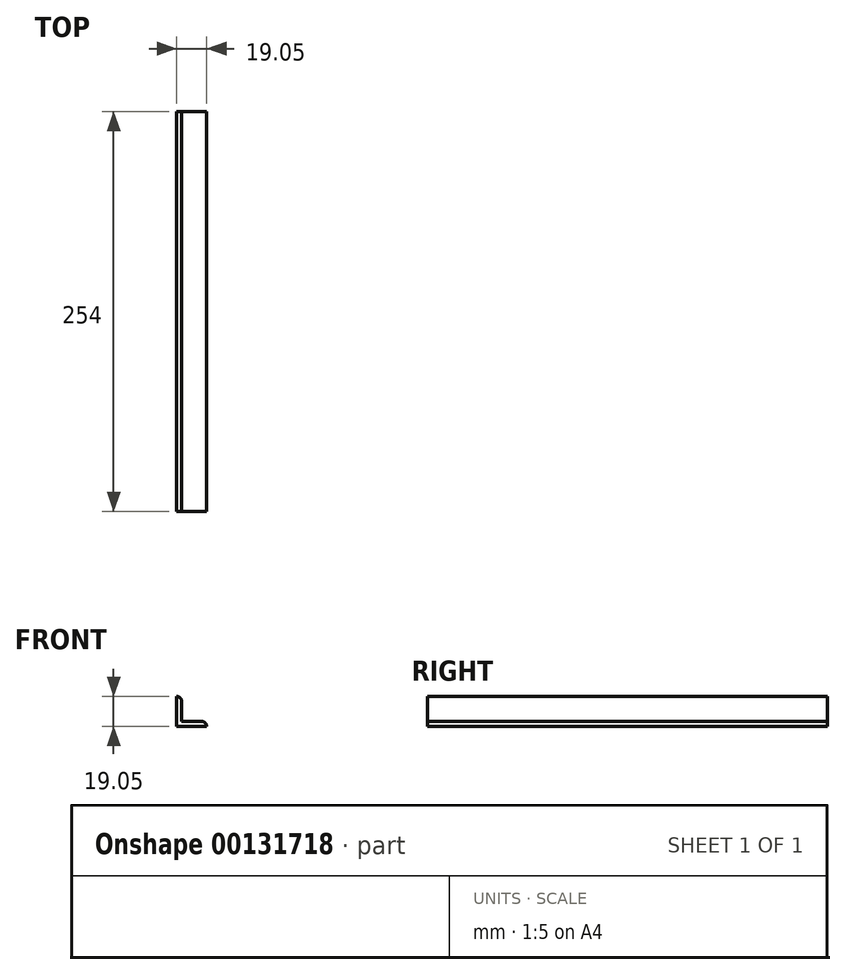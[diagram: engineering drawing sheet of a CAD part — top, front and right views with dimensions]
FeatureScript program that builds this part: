
annotation { "Feature Type Name" : "Feature", "Feature Type Description" : "" }
export const myFeature = defineFeature(function(context is Context, id is Id, definition is map)
    precondition{}
    {
        {
            var Q0;
            Q0=qCreatedBy(makeId("Front.planeOp"),FACE);
            var sketch = newSketch(context, id + "F0", { "sketchPlane" : qUnion([Q0])});
            skLineSegment(sketch, "E0", {"start": v(0, 19.05) * mm, "end": v(0, 0) * mm});
            skLineSegment(sketch, "E1", {"start": v(0, 0) * mm, "end": v(19.05, 0) * mm});
            skLineSegment(sketch, "E2", {"start": v(15.88, 3.17) * mm, "end": v(3.18, 3.17) * mm});
            skLineSegment(sketch, "E3", {"start": v(3.17, 3.17) * mm, "end": v(3.17, 15.88) * mm});
            skLineSegment(sketch, "E4", {"start": v(0, 19.05) * mm, "end": v(0, 19.05) * mm});
            skArc(sketch, "E5.filletArc", {"start": v(3.17, 15.88) * mm, "mid": v(2.25, 18.12) * mm, "end": v(0, 19.05) * mm});
            skArc(sketch, "E6.filletArc", {"start": v(19.05, 0) * mm, "mid": v(18.12, 2.25) * mm, "end": v(15.88, 3.18) * mm});
            skSolve(sketch);
        }
        {
            var Q0;
            Q0=makeQuery(id+"F0.imprint","IMPRINT",FACE,{"disambiguationData":[TD([[makeQuery(id+"F0.imprint","IMPRINT",EDGE,{"derivedFrom":sQuery(id+"F0.wireOp",EDGE,"E0")}),1.0]])]});
            extrude(context, id + "F1", {"entities" : qUnion([Q0]), "endBound" : BoundingType.SYMMETRIC, "depth" : 254 * mm});
        }
    });
